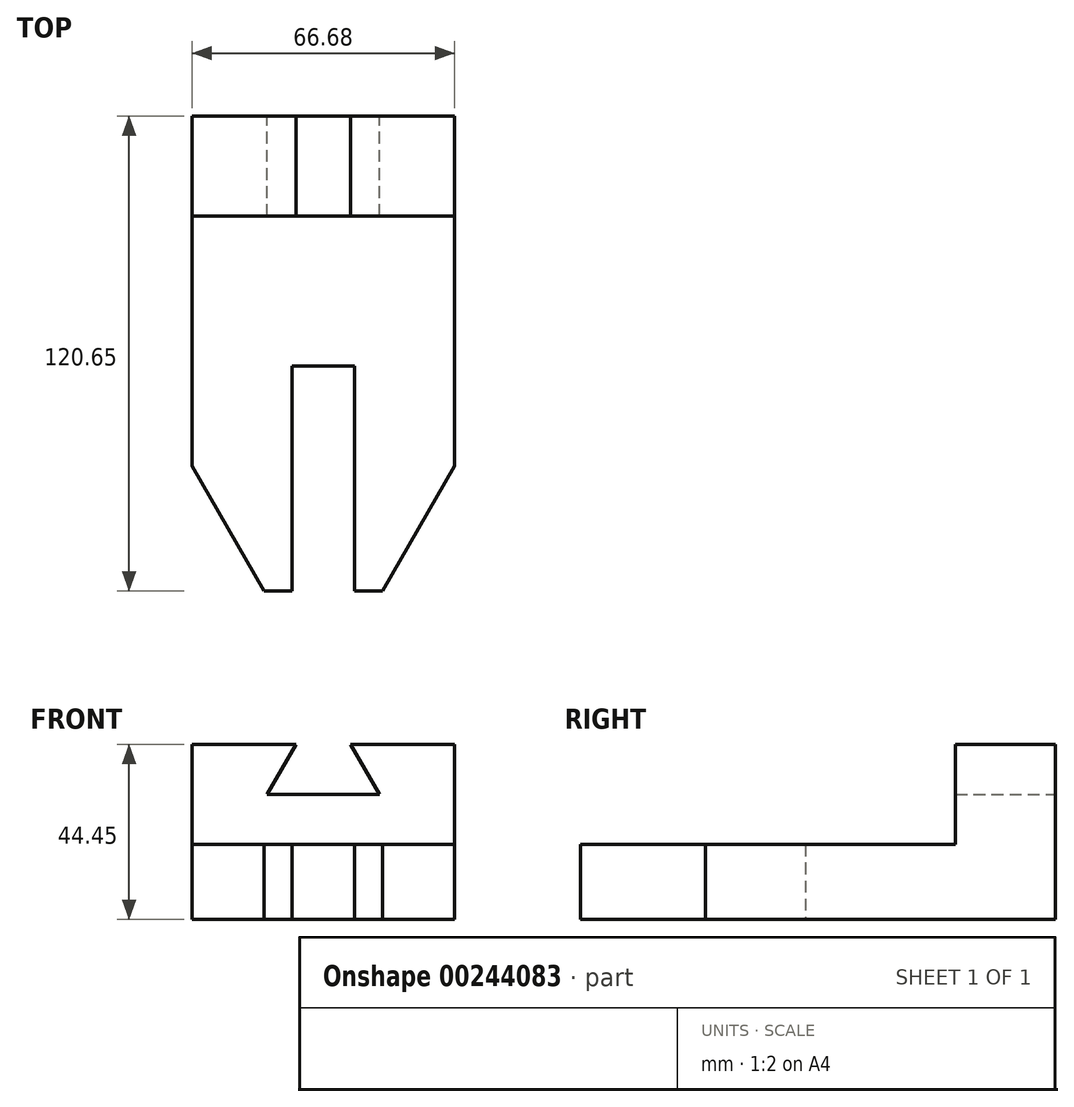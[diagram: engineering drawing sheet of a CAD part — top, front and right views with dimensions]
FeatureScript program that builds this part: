
annotation { "Feature Type Name" : "Feature", "Feature Type Description" : "" }
export const myFeature = defineFeature(function(context is Context, id is Id, definition is map)
    precondition{}
    {
        {
            var Q0;
            Q0=qCreatedBy(makeId("Top.planeOp"),FACE);
            var sketch = newSketch(context, id + "F0", { "sketchPlane" : qUnion([Q0])});
            skLineSegment(sketch, "E0", {"start": v(-27.95, 51.3) * mm, "end": v(-27.95, -37.6) * mm});
            skLineSegment(sketch, "E1", {"start": v(-9.61, -69.36) * mm, "end": v(-2.55, -69.36) * mm});
            skLineSegment(sketch, "E2", {"start": v(-2.55, -69.36) * mm, "end": v(-2.55, -12.2) * mm});
            skLineSegment(sketch, "E3", {"start": v(-2.55, -12.2) * mm, "end": v(13.33, -12.2) * mm});
            skLineSegment(sketch, "E4", {"start": v(13.33, -12.2) * mm, "end": v(13.33, -69.36) * mm});
            skLineSegment(sketch, "E5", {"start": v(13.33, -69.36) * mm, "end": v(20.4, -69.36) * mm});
            skLineSegment(sketch, "E6", {"start": v(38.73, -69.36) * mm, "end": v(38.73, -37.6) * mm});
            skLineSegment(sketch, "E7", {"start": v(38.73, -37.6) * mm, "end": v(38.73, 51.3) * mm});
            skLineSegment(sketch, "E8", {"start": v(38.73, 51.3) * mm, "end": v(-27.95, 51.3) * mm});
            skLineSegment(sketch, "E9", {"start": v(38.73, -37.6) * mm, "end": v(38.73, -69.36) * mm});
            skLineSegment(sketch, "E10", {"start": v(38.73, -69.36) * mm, "end": v(38.73, -69.36) * mm});
            skLineSegment(sketch, "E11", {"start": v(-27.95, -37.6) * mm, "end": v(-9.61, -69.36) * mm});
            skLineSegment(sketch, "E12", {"start": v(38.73, -37.6) * mm, "end": v(20.4, -69.36) * mm});
            skPoint(sketch, "E13.orphan", {"position": v(-27.95, -69.36) * mm});
            skSolve(sketch);
        }
        {
            var Q0;
            Q0 = qSketchRegion(id + "F0", true);
            extrude(context, id + "F1", {"entities" : qUnion([Q0]), "depth" : 19.05 * mm});
        }
        {
            var Q0;
            Q0=makeQuery(id+"F1.opExtrude","SWEPT_FACE",FACE,{"disambiguationData":[OSD([sQuery(id+"F0.wireOp",EDGE,"E8")])]});
            var sketch = newSketch(context, id + "F2", { "sketchPlane" : qUnion([Q0])});
            skLineSegment(sketch, "E14", {"start": v(-38.73, 19.05) * mm, "end": v(-38.73, 44.45) * mm});
            skLineSegment(sketch, "E15", {"start": v(-12.35, 44.45) * mm, "end": v(-38.73, 44.45) * mm});
            skLineSegment(sketch, "E16", {"start": v(1.56, 44.45) * mm, "end": v(8.9, 31.75) * mm});
            skLineSegment(sketch, "E17", {"start": v(8.9, 31.75) * mm, "end": v(-19.68, 31.75) * mm});
            skLineSegment(sketch, "E18", {"start": v(-19.68, 31.75) * mm, "end": v(-12.35, 44.45) * mm});
            skLineSegment(sketch, "E19", {"start": v(27.95, 44.45) * mm, "end": v(1.56, 44.45) * mm});
            skLineSegment(sketch, "E20", {"start": v(27.95, 44.45) * mm, "end": v(27.95, 19.05) * mm});
            skSolve(sketch);
        }
        {
            var Q0;
            Q0=makeQuery(id+"F2.imprint","IMPRINT",FACE,{"disambiguationData":[TD([[makeQuery(id+"F2.imprint","IMPRINT",EDGE,{"derivedFrom":sQuery(id+"F2.wireOp",EDGE,"E14")}),-1.0]])]});
            extrude(context, id + "F3", {"entities" : qUnion([Q0]), "operationType" : NewBodyOperationType.ADD, "oppositeDirection" : true, "depth" : 25.4 * mm});
        }
    });
